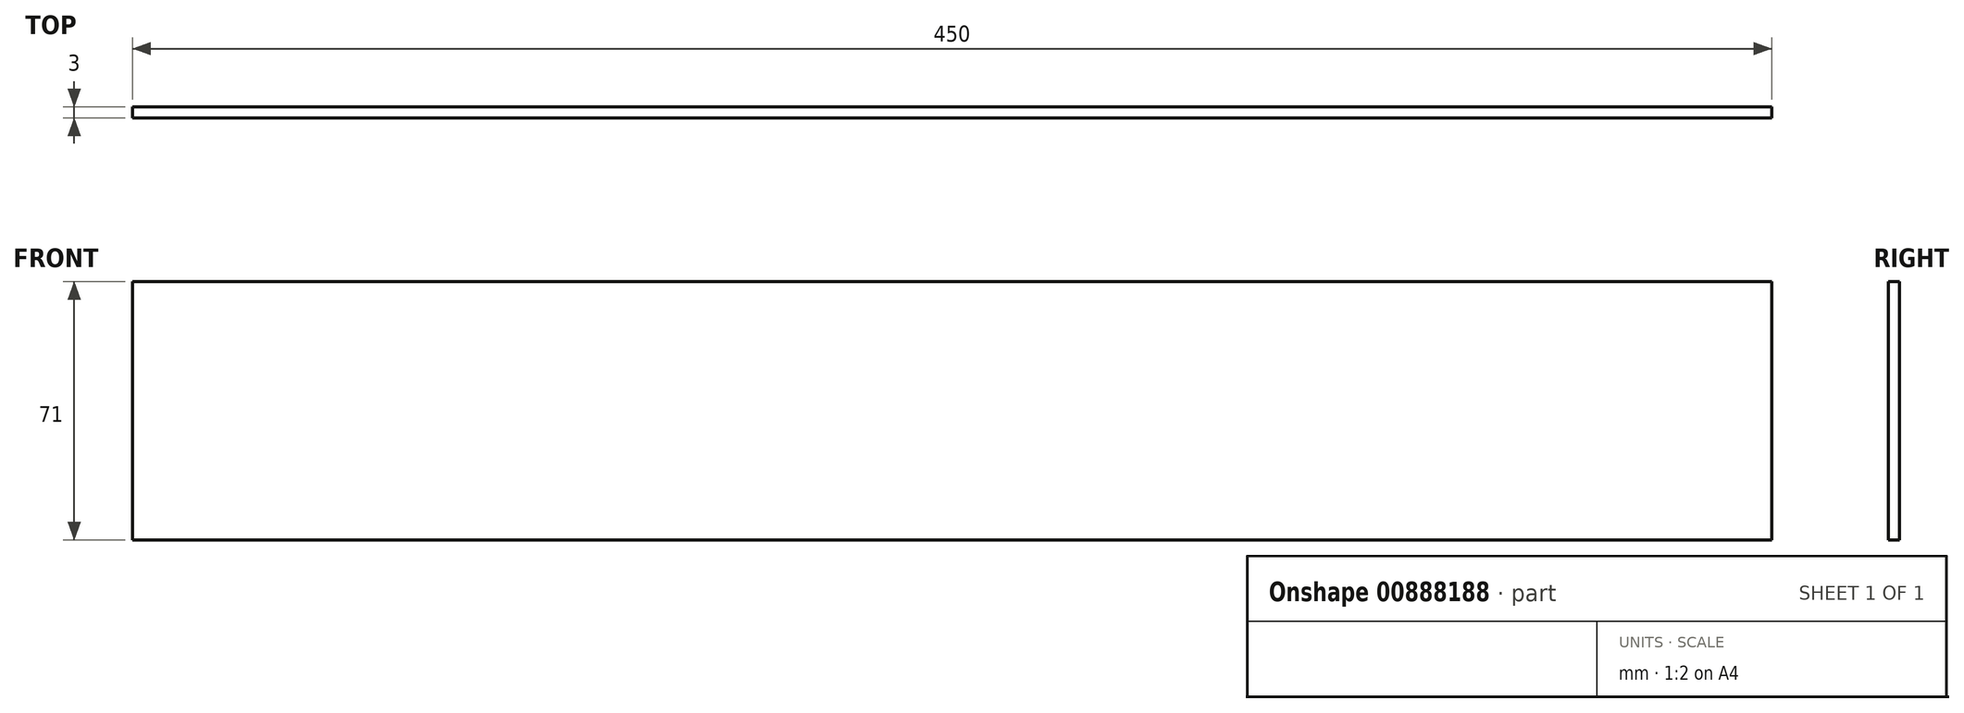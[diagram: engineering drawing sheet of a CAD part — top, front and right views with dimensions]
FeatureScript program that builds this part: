
annotation { "Feature Type Name" : "Feature", "Feature Type Description" : "" }
export const myFeature = defineFeature(function(context is Context, id is Id, definition is map)
    precondition{}
    {
        {
            var Q0;
            Q0=qCreatedBy(makeId("Front.planeOp"),FACE);
            var sketch = newSketch(context, id + "F0", { "sketchPlane" : qUnion([Q0])});
            skLineSegment(sketch, "E0.bottom", {"start": v(-350, 71) * mm, "end": v(100, 71) * mm});
            skLineSegment(sketch, "E0.top", {"start": v(-350, 0) * mm, "end": v(100, 0) * mm});
            skLineSegment(sketch, "E0.left", {"start": v(-350, 71) * mm, "end": v(-350, 0) * mm});
            skLineSegment(sketch, "E0.right", {"start": v(100, 71) * mm, "end": v(100, 0) * mm});
            skSolve(sketch);
        }
        {
            var Q0;
            Q0=makeQuery(id+"F0.imprint","IMPRINT",FACE,{"disambiguationData":[TD([[makeQuery(id+"F0.imprint","IMPRINT",EDGE,{"derivedFrom":sQuery(id+"F0.wireOp",EDGE,"E0.bottom")}),-1.0]])]});
            extrude(context, id + "F1", {"entities" : qUnion([Q0]), "endBound" : BoundingType.SYMMETRIC, "depth" : 3 * mm, "offsetDistance" : 25 * mm});
        }
    });
